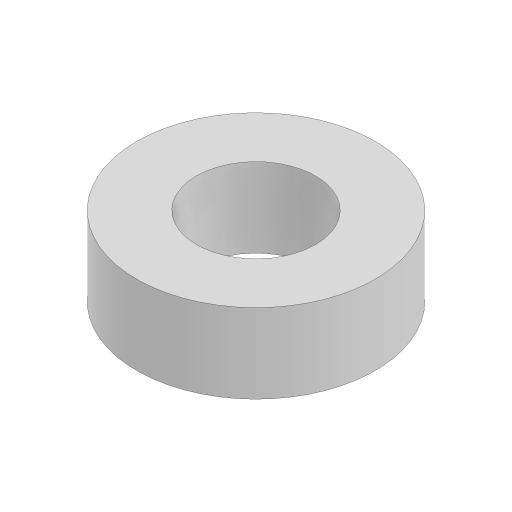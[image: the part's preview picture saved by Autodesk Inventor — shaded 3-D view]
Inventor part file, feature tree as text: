
AUTODESK INVENTOR PART (.ipt)
format: ipt  version: 2024 (Build 280153000, 153)  size: 99,840 bytes
history: native  units: mm
features: extrude x1, direct_edit x1, sketch x1, other x1
ambient origin geometry x8: Origin, YZ Plane, XZ Plane, XY Plane, X Axis, Y Axis, Z Axis, Center Point
bodies: Solid1 (feature_tree)
feature tree (4):
  extrude  "Extrusion1"  Depth=6.35mm
  direct_edit  "Direct Edit1"
  sketch  "Sketch1"  dims[d0=9.525mm d1=4.8mm d2=6.35mm d3=0.0mm d4=-0.01mm]
  other  "Size1"
